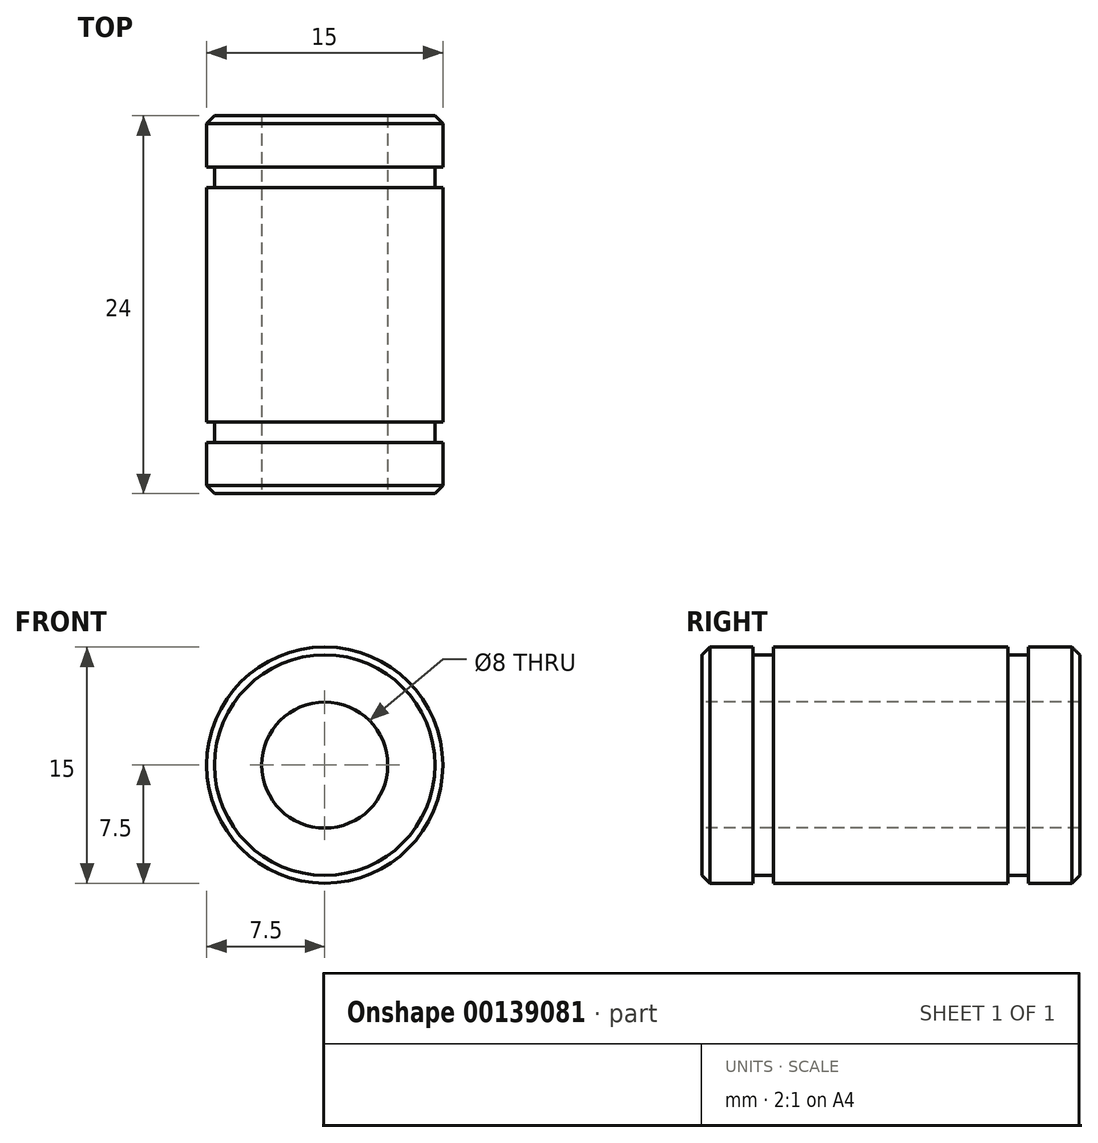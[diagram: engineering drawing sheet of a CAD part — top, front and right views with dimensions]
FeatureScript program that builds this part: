
annotation { "Feature Type Name" : "Feature", "Feature Type Description" : "" }
export const myFeature = defineFeature(function(context is Context, id is Id, definition is map)
    precondition{}
    {
        {
            var Q0;
            Q0=qCreatedBy(makeId("Right.planeOp"),FACE);
            var sketch = newSketch(context, id + "F0", { "sketchPlane" : qUnion([Q0])});
            skLineSegment(sketch, "E0", {"start": v(0, 0) * mm, "end": v(0, 4) * mm, "construction": true});
            skLineSegment(sketch, "E1", {"start": v(0, 4) * mm, "end": v(12, 4) * mm});
            skLineSegment(sketch, "E2", {"start": v(0, 4) * mm, "end": v(0, 7.5) * mm});
            skLineSegment(sketch, "E3", {"start": v(0, 7.5) * mm, "end": v(7.45, 7.5) * mm});
            skLineSegment(sketch, "E4", {"start": v(7.45, 7.5) * mm, "end": v(7.45, 7) * mm});
            skLineSegment(sketch, "E5", {"start": v(7.45, 7) * mm, "end": v(8.75, 7) * mm});
            skLineSegment(sketch, "E6", {"start": v(8.75, 7) * mm, "end": v(8.75, 7.5) * mm});
            skLineSegment(sketch, "E7", {"start": v(8.75, 7.5) * mm, "end": v(12, 7.5) * mm});
            skLineSegment(sketch, "E8", {"start": v(12, 7.5) * mm, "end": v(12, 4) * mm});
            skLineSegment(sketch, "E9", {"start": v(8.75, 7.5) * mm, "end": v(7.45, 7.5) * mm, "construction": true});
            skLineSegment(sketch, "E10", {"start": v(0, 0) * mm, "end": v(13.51, 0) * mm, "construction": true});
            skSolve(sketch);
        }
        {
            var Q0;
            Q0=makeQuery(id+"F0.imprint","IMPRINT",FACE,{"disambiguationData":[TD([[makeQuery(id+"F0.imprint","IMPRINT",EDGE,{"derivedFrom":sQuery(id+"F0.wireOp",EDGE,"E1")}),1.0]])]});
            var Q1;
            Q1=sQuery(id+"F0.wireOp",EDGE,"E10");
            revolve(context, id + "F1", {"entities" : qUnion([Q0]), "axis" : qUnion([Q1]), "revolveType" : RevolveType.FULL});
        }
        {
            var Q0;
            Q0=makeQuery(id+"F1.opRevolve","SWEPT_EDGE",EDGE,{"disambiguationData":[OSD([sQuery(id+"F0.wireOp",EDGE,"E7"),sQuery(id+"F0.wireOp",EDGE,"E8")])]});
            chamfer(context, id + "F2", {"entities" : qUnion([Q0]), "width" : 0.5 * mm, "tangentPropagation" : true});
        }
        {
            var Q0;
            Q0=makeQuery(id+"F1.opRevolve","SWEPT_BODY",BODY,{"disambiguationData":[OSD([sQuery(id+"F0.wireOp",EDGE,"E1"),sQuery(id+"F0.wireOp",EDGE,"E2"),sQuery(id+"F0.wireOp",EDGE,"E3"),sQuery(id+"F0.wireOp",EDGE,"E4"),sQuery(id+"F0.wireOp",EDGE,"E5"),sQuery(id+"F0.wireOp",EDGE,"E6"),sQuery(id+"F0.wireOp",EDGE,"E7"),sQuery(id+"F0.wireOp",EDGE,"E8")])]});
            var Q1;
            Q1=makeQuery(id+"F1.opRevolve","SWEPT_FACE",FACE,{"disambiguationData":[OSD([sQuery(id+"F0.wireOp",EDGE,"E2")])]});
            mirror(context, id + "F3", {"operationType" : NewBodyOperationType.ADD, "entities" : qUnion([Q0]), "mirrorPlane" : qUnion([Q1])});
        }
    });
